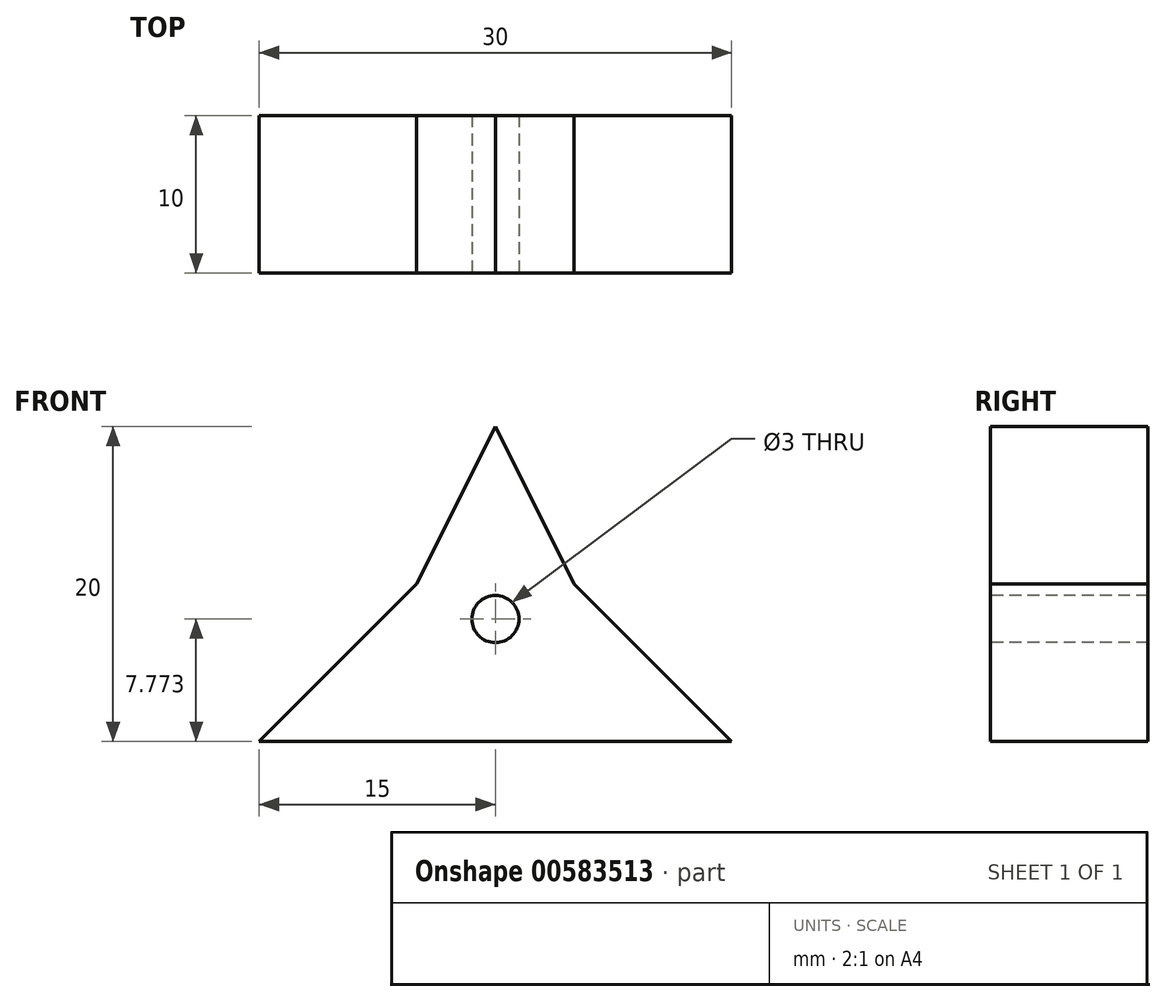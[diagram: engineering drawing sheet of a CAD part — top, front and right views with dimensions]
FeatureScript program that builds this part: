
annotation { "Feature Type Name" : "Feature", "Feature Type Description" : "" }
export const myFeature = defineFeature(function(context is Context, id is Id, definition is map)
    precondition{}
    {
        {
            var Q0;
            Q0=qCreatedBy(makeId("Top.planeOp"),FACE);
            var sketch = newSketch(context, id + "F0", { "sketchPlane" : qUnion([Q0])});
            skLineSegment(sketch, "E0.bottom", {"start": v(15, 5) * mm, "end": v(-15, 5) * mm});
            skLineSegment(sketch, "E0.top", {"start": v(15, -5) * mm, "end": v(-15, -5) * mm});
            skLineSegment(sketch, "E0.left", {"start": v(15, 5) * mm, "end": v(15, -5) * mm});
            skLineSegment(sketch, "E0.right", {"start": v(-15, 5) * mm, "end": v(-15, -5) * mm});
            skPoint(sketch, "E0.middle", {"position": v(0, 0) * mm});
            skSolve(sketch);
        }
        {
            var Q0;
            Q0=makeQuery(id+"F0.imprint","IMPRINT",FACE,{"disambiguationData":[TD([[makeQuery(id+"F0.imprint","IMPRINT",EDGE,{"derivedFrom":sQuery(id+"F0.wireOp",EDGE,"E0.bottom")}),1.0]])]});
            extrude(context, id + "F1", {"entities" : qUnion([Q0]), "depth" : 10 * mm, "offsetDistance" : 25 * mm});
        }
        {
            var Q0;
            Q0=makeQuery(id+"F1.opExtrude","CAP_FACE",FACE,{"disambiguationData":[OSD([sQuery(id+"F0.wireOp",EDGE,"E0.bottom"),sQuery(id+"F0.wireOp",EDGE,"E0.top"),sQuery(id+"F0.wireOp",EDGE,"E0.left"),sQuery(id+"F0.wireOp",EDGE,"E0.right")])],"isStart":false});
            var sketch = newSketch(context, id + "F2", { "sketchPlane" : qUnion([Q0])});
            skLineSegment(sketch, "E1.bottom", {"start": v(5, 5) * mm, "end": v(-5, 5) * mm});
            skLineSegment(sketch, "E1.top", {"start": v(5, -5) * mm, "end": v(-5, -5) * mm});
            skLineSegment(sketch, "E1.left", {"start": v(5, 5) * mm, "end": v(5, -5) * mm});
            skLineSegment(sketch, "E1.right", {"start": v(-5, 5) * mm, "end": v(-5, -5) * mm});
            skPoint(sketch, "E1.middle", {"position": v(0, 0) * mm});
            skSolve(sketch);
        }
        {
            var Q0;
            Q0=makeQuery(id+"F2.imprint","IMPRINT",FACE,{"disambiguationData":[TD([[makeQuery(id+"F2.imprint","IMPRINT",EDGE,{"derivedFrom":sQuery(id+"F2.wireOp",EDGE,"E1.bottom")}),1.0]])]});
            extrude(context, id + "F3", {"entities" : qUnion([Q0]), "operationType" : NewBodyOperationType.ADD, "depth" : 10 * mm, "offsetDistance" : 25 * mm});
        }
        {
            var Q0;
            Q0=makeQuery(id+"F3.boolean.opBoolean","MERGE",FACE,{"derivedFrom":[makeQuery(id+"F1.opExtrude","SWEPT_FACE",FACE,{"disambiguationData":[OSD([sQuery(id+"F0.wireOp",EDGE,"E0.top")])]}),makeQuery(id+"F3.opExtrude","SWEPT_FACE",FACE,{"disambiguationData":[OSD([sQuery(id+"F2.wireOp",EDGE,"E1.top")])]})]});
            var sketch = newSketch(context, id + "F4", { "sketchPlane" : qUnion([Q0])});
            skCircle(sketch, "E2", {"center": v(0, 7.77) * mm, "radius": 1.5 * mm});
            skSolve(sketch);
        }
        {
            var Q0;
            Q0=makeQuery(id+"F4.imprint","IMPRINT",FACE,{"disambiguationData":[TD([[makeQuery(id+"F4.imprint","IMPRINT",EDGE,{"derivedFrom":sQuery(id+"F4.wireOp",EDGE,"E2")}),1.0]])]});
            extrude(context, id + "F5", {"entities" : qUnion([Q0]), "operationType" : NewBodyOperationType.REMOVE, "endBound" : BoundingType.THROUGH_ALL, "oppositeDirection" : true, "depth" : 25 * mm, "offsetDistance" : 25 * mm});
        }
        {
            var Q0;
            Q0=makeQuery(id+"F3.boolean.opBoolean","MERGE",FACE,{"derivedFrom":[makeQuery(id+"F1.opExtrude","SWEPT_FACE",FACE,{"disambiguationData":[OSD([sQuery(id+"F0.wireOp",EDGE,"E0.top")])]}),makeQuery(id+"F3.opExtrude","SWEPT_FACE",FACE,{"disambiguationData":[OSD([sQuery(id+"F2.wireOp",EDGE,"E1.top")])]})]});
            var sketch = newSketch(context, id + "F6", { "sketchPlane" : qUnion([Q0])});
            skLineSegment(sketch, "E3", {"start": v(-5, 10) * mm, "end": v(0, 20) * mm});
            skLineSegment(sketch, "E4", {"start": v(0, 20) * mm, "end": v(5, 10) * mm});
            skLineSegment(sketch, "E5", {"start": v(-15, 0) * mm, "end": v(-5, 10) * mm});
            skLineSegment(sketch, "E6", {"start": v(5, 10) * mm, "end": v(15, 0) * mm});
            skSolve(sketch);
        }
        {
            var Q0;
            Q0=makeQuery(id+"F6.imprint","IMPRINT",FACE,{"disambiguationData":[TD([[makeQuery(id+"F6.imprint","IMPRINT",EDGE,{"derivedFrom":sQuery(id+"F6.wireOp",EDGE,"E5")}),1.0]])]});
            var Q1;
            {var subQ0=sQuery(id+"F6.wireOp",EDGE,"E3");Q1=makeQuery(id+"F6.imprint","IMPRINT",FACE,{"disambiguationData":[TD([[makeQuery(id+"F6.imprint","IMPRINT",EDGE,{"derivedFrom":subQ0}),1.0]])]});}
            var Q2;
            {var subQ0=sQuery(id+"F6.wireOp",EDGE,"E4");Q2=makeQuery(id+"F6.imprint","IMPRINT",FACE,{"disambiguationData":[TD([[makeQuery(id+"F6.imprint","IMPRINT",EDGE,{"derivedFrom":subQ0}),1.0]])]});}
            var Q3;
            Q3=makeQuery(id+"F6.imprint","IMPRINT",FACE,{"disambiguationData":[TD([[makeQuery(id+"F6.imprint","IMPRINT",EDGE,{"derivedFrom":sQuery(id+"F6.wireOp",EDGE,"E6")}),1.0]])]});
            extrude(context, id + "F7", {"entities" : qUnion([Q0, Q1, Q2, Q3]), "operationType" : NewBodyOperationType.REMOVE, "endBound" : BoundingType.THROUGH_ALL, "oppositeDirection" : true, "depth" : 25 * mm, "offsetDistance" : 25 * mm});
        }
    });
